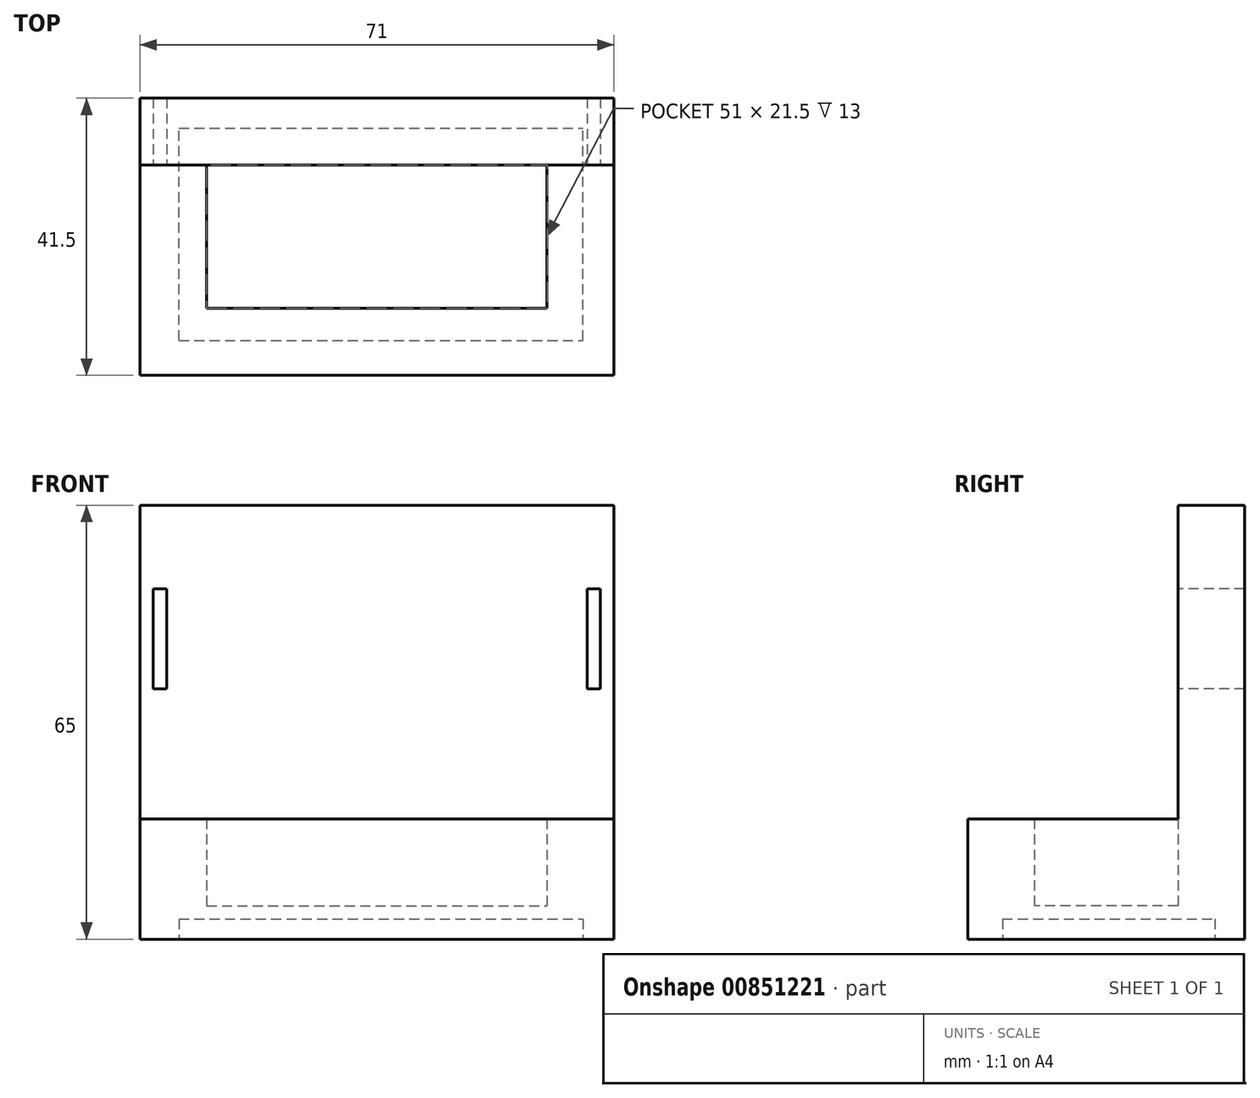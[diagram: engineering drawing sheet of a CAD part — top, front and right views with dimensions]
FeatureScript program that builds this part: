
annotation { "Feature Type Name" : "Feature", "Feature Type Description" : "" }
export const myFeature = defineFeature(function(context is Context, id is Id, definition is map)
    precondition{}
    {
        {
            var Q0;
            Q0=qCreatedBy(makeId("Top.planeOp"),FACE);
            var sketch = newSketch(context, id + "F0", { "sketchPlane" : qUnion([Q0])});
            skLineSegment(sketch, "E0.bottom", {"start": v(-27.3, 13.42) * mm, "end": v(23.7, 13.42) * mm});
            skLineSegment(sketch, "E0.top", {"start": v(-27.3, -8.08) * mm, "end": v(23.7, -8.08) * mm});
            skLineSegment(sketch, "E0.left", {"start": v(-27.3, 13.42) * mm, "end": v(-27.3, -8.08) * mm});
            skLineSegment(sketch, "E0.right", {"start": v(23.7, 13.42) * mm, "end": v(23.7, -8.08) * mm});
            skLineSegment(sketch, "E1", {"start": v(-27.3, 13.42) * mm, "end": v(-27.3, 23.42) * mm, "construction": true});
            skLineSegment(sketch, "E2", {"start": v(-27.3, 23.42) * mm, "end": v(23.7, 23.42) * mm});
            skLineSegment(sketch, "E3", {"start": v(23.7, 23.42) * mm, "end": v(23.7, 13.42) * mm, "construction": true});
            skLineSegment(sketch, "E4", {"start": v(23.7, 23.42) * mm, "end": v(33.7, 23.42) * mm});
            skLineSegment(sketch, "E5", {"start": v(33.7, 23.42) * mm, "end": v(33.7, 13.42) * mm});
            skLineSegment(sketch, "E6", {"start": v(33.7, 13.42) * mm, "end": v(33.7, -8.08) * mm});
            skLineSegment(sketch, "E7", {"start": v(33.7, -8.08) * mm, "end": v(33.7, -18.08) * mm});
            skLineSegment(sketch, "E8", {"start": v(33.7, -18.08) * mm, "end": v(23.7, -18.08) * mm});
            skLineSegment(sketch, "E9", {"start": v(23.7, -18.08) * mm, "end": v(-27.3, -18.08) * mm});
            skLineSegment(sketch, "E10", {"start": v(-27.3, -18.08) * mm, "end": v(-37.3, -18.08) * mm});
            skLineSegment(sketch, "E11", {"start": v(-37.3, -18.08) * mm, "end": v(-37.3, -8.08) * mm});
            skLineSegment(sketch, "E12", {"start": v(-37.3, -8.08) * mm, "end": v(-37.3, 13.42) * mm});
            skLineSegment(sketch, "E13", {"start": v(-37.3, 13.42) * mm, "end": v(-37.3, 23.42) * mm});
            skLineSegment(sketch, "E14", {"start": v(-37.3, 23.42) * mm, "end": v(-27.3, 23.42) * mm});
            skLineSegment(sketch, "E15", {"start": v(-27.3, -8.08) * mm, "end": v(-27.3, -18.08) * mm, "construction": true});
            skLineSegment(sketch, "E16", {"start": v(23.7, 13.42) * mm, "end": v(33.7, 13.42) * mm});
            skLineSegment(sketch, "E17", {"start": v(-27.3, -8.08) * mm, "end": v(-37.3, -8.08) * mm, "construction": true});
            skLineSegment(sketch, "E18", {"start": v(-27.3, 13.42) * mm, "end": v(-37.3, 13.42) * mm});
            skSolve(sketch);
        }
        {
            var Q0;
            Q0=makeQuery(id+"F0.imprint","IMPRINT",FACE,{"disambiguationData":[TD([[makeQuery(id+"F0.imprint","IMPRINT",EDGE,{"derivedFrom":sQuery(id+"F0.wireOp",EDGE,"E0.bottom")}),1.0]])]});
            var Q1;
            Q1=makeQuery(id+"F0.imprint","IMPRINT",FACE,{"disambiguationData":[TD([[makeQuery(id+"F0.imprint","IMPRINT",EDGE,{"derivedFrom":sQuery(id+"F0.wireOp",EDGE,"E0.top")}),-1.0]])]});
            extrude(context, id + "F1", {"entities" : qUnion([Q0, Q1]), "depth" : 18 * mm, "offsetDistance" : 25 * mm});
        }
        {
            var Q0;
            Q0=makeQuery(id+"F0.imprint","IMPRINT",FACE,{"disambiguationData":[TD([[makeQuery(id+"F0.imprint","IMPRINT",EDGE,{"derivedFrom":sQuery(id+"F0.wireOp",EDGE,"E0.bottom")}),-1.0]])]});
            extrude(context, id + "F2", {"entities" : qUnion([Q0]), "operationType" : NewBodyOperationType.ADD, "depth" : 5 * mm, "offsetDistance" : 25 * mm});
        }
        {
            var Q0;
            Q0=makeQuery(id+"F1.opExtrude","CAP_FACE",FACE,{"disambiguationData":[OSD([sQuery(id+"F0.wireOp",EDGE,"E0.bottom"),sQuery(id+"F0.wireOp",EDGE,"E0.top"),sQuery(id+"F0.wireOp",EDGE,"E0.left"),sQuery(id+"F0.wireOp",EDGE,"E0.right"),sQuery(id+"F0.wireOp",EDGE,"E2"),sQuery(id+"F0.wireOp",EDGE,"E4"),sQuery(id+"F0.wireOp",EDGE,"E5"),sQuery(id+"F0.wireOp",EDGE,"E6"),sQuery(id+"F0.wireOp",EDGE,"E7"),sQuery(id+"F0.wireOp",EDGE,"E8"),sQuery(id+"F0.wireOp",EDGE,"E9"),sQuery(id+"F0.wireOp",EDGE,"E10"),sQuery(id+"F0.wireOp",EDGE,"E11"),sQuery(id+"F0.wireOp",EDGE,"E12"),sQuery(id+"F0.wireOp",EDGE,"E13"),sQuery(id+"F0.wireOp",EDGE,"E14")])],"isStart":false});
            var sketch = newSketch(context, id + "F3", { "sketchPlane" : qUnion([Q0])});
            skLineSegment(sketch, "E19.bottom", {"start": v(-37.3, 23.42) * mm, "end": v(33.7, 23.42) * mm});
            skLineSegment(sketch, "E19.top", {"start": v(-37.3, 13.42) * mm, "end": v(33.7, 13.42) * mm});
            skLineSegment(sketch, "E19.left", {"start": v(-37.3, 23.42) * mm, "end": v(-37.3, 13.42) * mm});
            skLineSegment(sketch, "E19.right", {"start": v(33.7, 23.42) * mm, "end": v(33.7, 13.42) * mm});
            skSolve(sketch);
        }
        {
            var Q0;
            Q0=makeQuery(id+"F3.imprint","IMPRINT",FACE,{"disambiguationData":[TD([[makeQuery(id+"F3.imprint","IMPRINT",EDGE,{"derivedFrom":sQuery(id+"F3.wireOp",EDGE,"E19.bottom")}),-1.0]])]});
            extrude(context, id + "F4", {"entities" : qUnion([Q0]), "operationType" : NewBodyOperationType.ADD, "depth" : 47 * mm, "offsetDistance" : 25 * mm});
        }
        {
            var Q0;
            Q0=makeQuery(id+"F4.boolean.opBoolean","MERGE",FACE,{"derivedFrom":[makeQuery(id+"F1.opExtrude","SWEPT_FACE",FACE,{"disambiguationData":[OSD([sQuery(id+"F0.wireOp",EDGE,"E0.bottom")])]}),makeQuery(id+"F4.opExtrude","SWEPT_FACE",FACE,{"disambiguationData":[OSD([sQuery(id+"F3.wireOp",EDGE,"E19.top")])]})]});
            var sketch = newSketch(context, id + "F5", { "sketchPlane" : qUnion([Q0])});
            skLineSegment(sketch, "E20", {"start": v(-37.3, 18) * mm, "end": v(-37.3, 50) * mm});
            skLineSegment(sketch, "E21", {"start": v(-37.3, 50) * mm, "end": v(-33.3, 50) * mm, "construction": true});
            skLineSegment(sketch, "E22", {"start": v(-33.3, 50) * mm, "end": v(29.7, 50) * mm});
            skLineSegment(sketch, "E23", {"start": v(29.7, 50) * mm, "end": v(33.7, 50) * mm});
            skLineSegment(sketch, "E24", {"start": v(33.7, 50) * mm, "end": v(33.7, 18) * mm});
            skLineSegment(sketch, "E25", {"start": v(-33.3, 50) * mm, "end": v(-33.3, 52.5) * mm});
            skLineSegment(sketch, "E26", {"start": v(-33.3, 50) * mm, "end": v(-33.3, 37.5) * mm});
            skLineSegment(sketch, "E27", {"start": v(-33.3, 52.5) * mm, "end": v(-35.3, 52.5) * mm});
            skLineSegment(sketch, "E28", {"start": v(-35.3, 52.5) * mm, "end": v(-35.3, 37.5) * mm});
            skLineSegment(sketch, "E29", {"start": v(-35.3, 37.5) * mm, "end": v(-33.3, 37.5) * mm});
            skLineSegment(sketch, "E30", {"start": v(29.7, 50) * mm, "end": v(29.7, 52.5) * mm});
            skLineSegment(sketch, "E31", {"start": v(29.7, 52.5) * mm, "end": v(31.7, 52.5) * mm});
            skLineSegment(sketch, "E32", {"start": v(31.7, 52.5) * mm, "end": v(31.7, 37.5) * mm});
            skLineSegment(sketch, "E33", {"start": v(31.7, 37.5) * mm, "end": v(29.7, 37.5) * mm});
            skLineSegment(sketch, "E34", {"start": v(29.7, 37.5) * mm, "end": v(29.7, 50) * mm});
            skSolve(sketch);
        }
        {
            var Q0;
            Q0=makeQuery(id+"F5.imprint","IMPRINT",FACE,{"disambiguationData":[TD([[makeQuery(id+"F5.imprint","IMPRINT",EDGE,{"derivedFrom":sQuery(id+"F5.wireOp",EDGE,"E25")}),1.0]])]});
            var Q1;
            {var subQ4=sQuery(id+"F5.wireOp",EDGE,"E33");Q1=makeQuery(id+"F5.imprint","IMPRINT",FACE,{"disambiguationData":[TD([[makeQuery(id+"F5.imprint","IMPRINT",EDGE,{"derivedFrom":subQ4}),-1.0]])]});}
            var Q2;
            {var subQ0=sQuery(id+"F5.wireOp",EDGE,"E30");Q2=makeQuery(id+"F5.imprint","IMPRINT",FACE,{"disambiguationData":[TD([[makeQuery(id+"F5.imprint","IMPRINT",EDGE,{"derivedFrom":subQ0}),-1.0]])]});}
            extrude(context, id + "F6", {"entities" : qUnion([Q0, Q1, Q2]), "operationType" : NewBodyOperationType.REMOVE, "oppositeDirection" : true, "depth" : 10 * mm, "offsetDistance" : 25 * mm});
        }
        {
            var Q0;
            {var subQ0=sQuery(id+"F0.wireOp",EDGE,"E0.right");var subQ1=sQuery(id+"F0.wireOp",EDGE,"E0.left");var subQ2=sQuery(id+"F0.wireOp",EDGE,"E0.top");var subQ3=sQuery(id+"F0.wireOp",EDGE,"E0.bottom");Q0=makeQuery(id+"F2.boolean.opBoolean","MERGE",FACE,{"derivedFrom":[makeQuery(id+"F1.opExtrude","CAP_FACE",FACE,{"disambiguationData":[OSD([subQ3,subQ2,subQ1,subQ0,sQuery(id+"F0.wireOp",EDGE,"E2"),sQuery(id+"F0.wireOp",EDGE,"E4"),sQuery(id+"F0.wireOp",EDGE,"E5"),sQuery(id+"F0.wireOp",EDGE,"E6"),sQuery(id+"F0.wireOp",EDGE,"E7"),sQuery(id+"F0.wireOp",EDGE,"E8"),sQuery(id+"F0.wireOp",EDGE,"E9"),sQuery(id+"F0.wireOp",EDGE,"E10"),sQuery(id+"F0.wireOp",EDGE,"E11"),sQuery(id+"F0.wireOp",EDGE,"E12"),sQuery(id+"F0.wireOp",EDGE,"E13"),sQuery(id+"F0.wireOp",EDGE,"E14")])],"isStart":true}),makeQuery(id+"F2.opExtrude","CAP_FACE",FACE,{"disambiguationData":[OSD([subQ3,subQ2,subQ1,subQ0])],"isStart":true})]});}
            var sketch = newSketch(context, id + "F7", { "sketchPlane" : qUnion([Q0])});
            skLineSegment(sketch, "E35.bottom", {"start": v(-31.43, 12.86) * mm, "end": v(29.07, 12.86) * mm});
            skLineSegment(sketch, "E35.top", {"start": v(-31.43, -18.96) * mm, "end": v(29.07, -18.96) * mm});
            skLineSegment(sketch, "E35.left", {"start": v(-31.43, 12.86) * mm, "end": v(-31.43, -18.96) * mm});
            skLineSegment(sketch, "E35.right", {"start": v(29.07, 12.86) * mm, "end": v(29.07, -18.96) * mm});
            skSolve(sketch);
        }
        {
            var Q0;
            Q0=makeQuery(id+"F7.imprint","IMPRINT",FACE,{"disambiguationData":[TD([[makeQuery(id+"F7.imprint","IMPRINT",EDGE,{"derivedFrom":sQuery(id+"F7.wireOp",EDGE,"E35.bottom")}),-1.0]])]});
            extrude(context, id + "F8", {"entities" : qUnion([Q0]), "operationType" : NewBodyOperationType.REMOVE, "oppositeDirection" : true, "depth" : 3 * mm, "offsetDistance" : 25 * mm});
        }
    });
